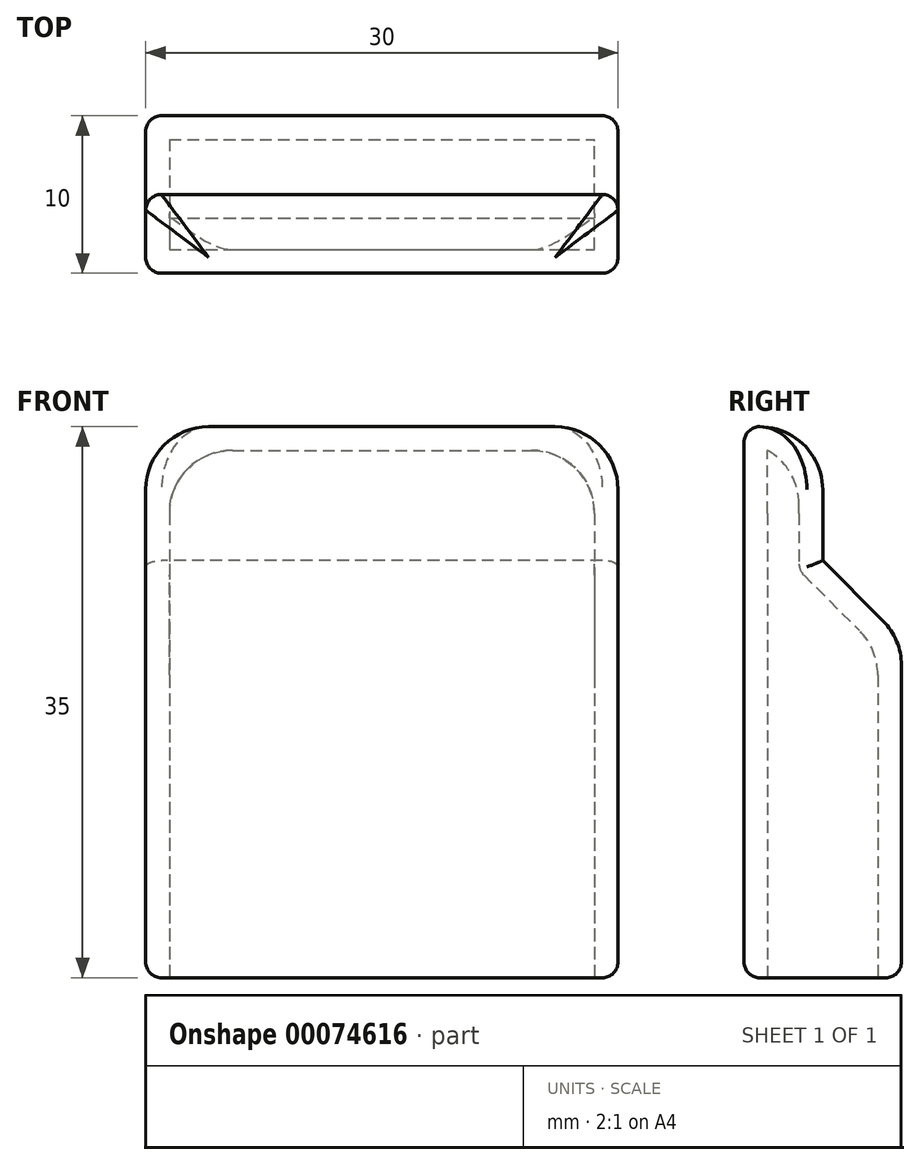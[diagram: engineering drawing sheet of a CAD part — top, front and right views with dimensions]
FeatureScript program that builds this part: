
annotation { "Feature Type Name" : "Feature", "Feature Type Description" : "" }
export const myFeature = defineFeature(function(context is Context, id is Id, definition is map)
    precondition{}
    {
        {
            var Q0;
            Q0=qCreatedBy(makeId("Top.planeOp"),FACE);
            var sketch = newSketch(context, id + "F0", { "sketchPlane" : qUnion([Q0])});
            skLineSegment(sketch, "E0", {"start": v(0, 0) * mm, "end": v(30, 0) * mm});
            skLineSegment(sketch, "E1", {"start": v(30, 0) * mm, "end": v(30, 5) * mm});
            skLineSegment(sketch, "E2", {"start": v(30, 5) * mm, "end": v(0, 5) * mm});
            skLineSegment(sketch, "E3", {"start": v(0, 5) * mm, "end": v(0, 0) * mm});
            skLineSegment(sketch, "E4", {"start": v(0, 5) * mm, "end": v(0, 10) * mm});
            skLineSegment(sketch, "E5", {"start": v(0, 10) * mm, "end": v(30, 10) * mm});
            skLineSegment(sketch, "E6", {"start": v(30, 10) * mm, "end": v(30, 5) * mm});
            skSolve(sketch);
        }
        {
            var Q0;
            Q0=makeQuery(id+"F0.imprint","IMPRINT",FACE,{"disambiguationData":[TD([[makeQuery(id+"F0.imprint","IMPRINT",EDGE,{"derivedFrom":sQuery(id+"F0.wireOp",EDGE,"E0")}),1.0]])]});
            extrude(context, id + "F1", {"entities" : qUnion([Q0]), "depth" : 35 * mm});
        }
        {
            var Q0;
            Q0=makeQuery(id+"F0.imprint","IMPRINT",FACE,{"disambiguationData":[TD([[makeQuery(id+"F0.imprint","IMPRINT",EDGE,{"derivedFrom":sQuery(id+"F0.wireOp",EDGE,"E2")}),-1.0]])]});
            extrude(context, id + "F2", {"entities" : qUnion([Q0]), "operationType" : NewBodyOperationType.ADD, "depth" : 26.5 * mm});
        }
        {
            var Q0;
            Q0=makeQuery(id+"F2.opExtrude","CAP_EDGE",EDGE,{"disambiguationData":[OSD([sQuery(id+"F0.wireOp",EDGE,"E5")])],"isStart":false});
            chamfer(context, id + "F3", {"entities" : qUnion([Q0]), "width" : 5 * mm, "tangentPropagation" : true});
        }
        {
            var Q0;
            {var subQ0=sQuery(id+"F0.wireOp",EDGE,"E2");Q0=makeQuery(id+"F2.boolean.opBoolean","MERGE",FACE,{"derivedFrom":[makeQuery(id+"F1.opExtrude","CAP_FACE",FACE,{"disambiguationData":[OSD([sQuery(id+"F0.wireOp",EDGE,"E0"),sQuery(id+"F0.wireOp",EDGE,"E1"),subQ0,sQuery(id+"F0.wireOp",EDGE,"E3")])],"isStart":true}),makeQuery(id+"F2.opExtrude","CAP_FACE",FACE,{"disambiguationData":[OSD([subQ0,sQuery(id+"F0.wireOp",EDGE,"E4"),sQuery(id+"F0.wireOp",EDGE,"E5"),sQuery(id+"F0.wireOp",EDGE,"E6")])],"isStart":true})]});}
            shell(context, id + "F4", {"entities" : qUnion([Q0]), "thickness" : 1.5 * mm});
        }
        {
            var Q0;
            Q0=makeQuery(id+"F1.opExtrude","CAP_EDGE",EDGE,{"disambiguationData":[OSD([sQuery(id+"F0.wireOp",EDGE,"E1")])],"isStart":false});
            var Q1;
            Q1=makeQuery(id+"F1.opExtrude","CAP_EDGE",EDGE,{"disambiguationData":[OSD([sQuery(id+"F0.wireOp",EDGE,"E3")])],"isStart":false});
            var Q2;
            {var subQ0=sQuery(id+"F0.wireOp",EDGE,"E5");Q2=makeQuery(id+"F3.opChamfer","BLEND_EDGE",EDGE,{"blendedFrom":[makeQuery(id+"F2.opExtrude","CAP_EDGE",EDGE,{"disambiguationData":[OSD([subQ0])],"isStart":false}),makeQuery(id+"F2.opExtrude","SWEPT_FACE",FACE,{"disambiguationData":[OSD([subQ0])]})],"blendedInto":[makeQuery(id+"F2.opExtrude","SWEPT_FACE",FACE,{"disambiguationData":[OSD([subQ0])]})]});}
            var Q3;
            {var subQ0=sQuery(id+"F0.wireOp",EDGE,"E5");Q3=makeQuery(id+"F4.opShell","OFFSET_EDGE",EDGE,{"disambiguationData":[OSD([subQ0]),TDD([makeQuery(id+"F3.opChamfer","BLEND_EDGE",EDGE,{"blendedFrom":[makeQuery(id+"F2.opExtrude","CAP_EDGE",EDGE,{"disambiguationData":[OSD([subQ0])],"isStart":false}),makeQuery(id+"F2.opExtrude","SWEPT_FACE",FACE,{"disambiguationData":[OSD([subQ0])]})],"blendedInto":[makeQuery(id+"F2.opExtrude","SWEPT_FACE",FACE,{"disambiguationData":[OSD([subQ0])]})]})])]});}
            var Q4;
            Q4=makeQuery(id+"F4.opShell","OFFSET_EDGE",EDGE,{"disambiguationData":[OSD([sQuery(id+"F0.wireOp",EDGE,"E1")])]});
            var Q5;
            Q5=makeQuery(id+"F4.opShell","OFFSET_EDGE",EDGE,{"disambiguationData":[OSD([sQuery(id+"F0.wireOp",EDGE,"E3")])]});
            fillet(context, id + "F5", {"entities" : qUnion([Q0, Q1, Q2, Q3, Q4, Q5]), "radius" : 4 * mm, "tangentPropagation" : true, "allowEdgeOverflow" : false});
        }
        {
            var Q0;
            Q0=makeQuery(id+"F1.opExtrude","CAP_EDGE",EDGE,{"disambiguationData":[OSD([sQuery(id+"F0.wireOp",EDGE,"E2")])],"isStart":false});
            var Q1;
            Q1=makeQuery(id+"F4.opShell","OFFSET_EDGE",EDGE,{"disambiguationData":[OSD([sQuery(id+"F0.wireOp",EDGE,"E2")])]});
            fillet(context, id + "F6", {"entities" : qUnion([Q0, Q1]), "radius" : 4 * mm, "allowEdgeOverflow" : false});
        }
        {
            var Q0;
            Q0=makeQuery(id+"F1.opExtrude","CAP_EDGE",EDGE,{"disambiguationData":[OSD([sQuery(id+"F0.wireOp",EDGE,"E0")])],"isStart":false});
            var Q1;
            Q1=makeQuery(id+"F5.opFillet","BLEND_EDGE",EDGE,{"blendedFrom":[makeQuery(id+"F1.opExtrude","CAP_EDGE",EDGE,{"disambiguationData":[OSD([sQuery(id+"F0.wireOp",EDGE,"E1")])],"isStart":false}),makeQuery(id+"F1.opExtrude","SWEPT_FACE",FACE,{"disambiguationData":[OSD([sQuery(id+"F0.wireOp",EDGE,"E0")])]})],"blendedInto":[makeQuery(id+"F1.opExtrude","SWEPT_FACE",FACE,{"disambiguationData":[OSD([sQuery(id+"F0.wireOp",EDGE,"E0")])]})]});
            var Q2;
            {var subQ0=sQuery(id+"F0.wireOp",EDGE,"E1");Q2=makeQuery(id+"F6.opFillet","BLEND_EDGE",EDGE,{"blendedFrom":[makeQuery(id+"F1.opExtrude","CAP_EDGE",EDGE,{"disambiguationData":[OSD([sQuery(id+"F0.wireOp",EDGE,"E2")])],"isStart":false}),makeQuery(id+"F5.opFillet","BLEND_FACE",FACE,{"disambiguationData":[OSD([subQ0]),TDD([makeQuery(id+"F1.opExtrude","CAP_EDGE",EDGE,{"disambiguationData":[OSD([subQ0])],"isStart":false})])]})],"blendedInto":[makeQuery(id+"F5.opFillet","BLEND_FACE",FACE,{"disambiguationData":[OSD([subQ0]),TDD([makeQuery(id+"F1.opExtrude","CAP_EDGE",EDGE,{"disambiguationData":[OSD([subQ0])],"isStart":false})])]})]});}
            var Q3;
            Q3=makeQuery(id+"F3.opChamfer","BLEND_EDGE",EDGE,{"blendedFrom":[makeQuery(id+"F2.opExtrude","CAP_EDGE",EDGE,{"disambiguationData":[OSD([sQuery(id+"F0.wireOp",EDGE,"E5")])],"isStart":false}),makeQuery(id+"F2.boolean.opBoolean","MERGE",FACE,{"derivedFrom":[makeQuery(id+"F1.opExtrude","SWEPT_FACE",FACE,{"disambiguationData":[OSD([sQuery(id+"F0.wireOp",EDGE,"E1")])]}),makeQuery(id+"F2.opExtrude","SWEPT_FACE",FACE,{"disambiguationData":[OSD([sQuery(id+"F0.wireOp",EDGE,"E6")])]})]})],"blendedInto":[makeQuery(id+"F2.boolean.opBoolean","MERGE",FACE,{"derivedFrom":[makeQuery(id+"F1.opExtrude","SWEPT_FACE",FACE,{"disambiguationData":[OSD([sQuery(id+"F0.wireOp",EDGE,"E1")])]}),makeQuery(id+"F2.opExtrude","SWEPT_FACE",FACE,{"disambiguationData":[OSD([sQuery(id+"F0.wireOp",EDGE,"E6")])]})]})]});
            var Q4;
            Q4=makeQuery(id+"F2.boolean.opBoolean","MERGE",EDGE,{"derivedFrom":[makeQuery(id+"F1.opExtrude","CAP_EDGE",EDGE,{"disambiguationData":[OSD([sQuery(id+"F0.wireOp",EDGE,"E1")])],"isStart":true}),makeQuery(id+"F2.opExtrude","CAP_EDGE",EDGE,{"disambiguationData":[OSD([sQuery(id+"F0.wireOp",EDGE,"E6")])],"isStart":true})]});
            var Q5;
            {var subQ0=sQuery(id+"F0.wireOp",EDGE,"E3");Q5=makeQuery(id+"F6.opFillet","BLEND_EDGE",EDGE,{"blendedFrom":[makeQuery(id+"F1.opExtrude","CAP_EDGE",EDGE,{"disambiguationData":[OSD([sQuery(id+"F0.wireOp",EDGE,"E2")])],"isStart":false}),makeQuery(id+"F5.opFillet","BLEND_FACE",FACE,{"disambiguationData":[OSD([subQ0]),TDD([makeQuery(id+"F1.opExtrude","CAP_EDGE",EDGE,{"disambiguationData":[OSD([subQ0])],"isStart":false})])]})],"blendedInto":[makeQuery(id+"F5.opFillet","BLEND_FACE",FACE,{"disambiguationData":[OSD([subQ0]),TDD([makeQuery(id+"F1.opExtrude","CAP_EDGE",EDGE,{"disambiguationData":[OSD([subQ0])],"isStart":false})])]})]});}
            var Q6;
            Q6=makeQuery(id+"F3.opChamfer","BLEND_EDGE",EDGE,{"blendedFrom":[makeQuery(id+"F2.opExtrude","CAP_EDGE",EDGE,{"disambiguationData":[OSD([sQuery(id+"F0.wireOp",EDGE,"E5")])],"isStart":false}),makeQuery(id+"F2.boolean.opBoolean","MERGE",FACE,{"derivedFrom":[makeQuery(id+"F1.opExtrude","SWEPT_FACE",FACE,{"disambiguationData":[OSD([sQuery(id+"F0.wireOp",EDGE,"E3")])]}),makeQuery(id+"F2.opExtrude","SWEPT_FACE",FACE,{"disambiguationData":[OSD([sQuery(id+"F0.wireOp",EDGE,"E4")])]})]})],"blendedInto":[makeQuery(id+"F2.boolean.opBoolean","MERGE",FACE,{"derivedFrom":[makeQuery(id+"F1.opExtrude","SWEPT_FACE",FACE,{"disambiguationData":[OSD([sQuery(id+"F0.wireOp",EDGE,"E3")])]}),makeQuery(id+"F2.opExtrude","SWEPT_FACE",FACE,{"disambiguationData":[OSD([sQuery(id+"F0.wireOp",EDGE,"E4")])]})]})]});
            var Q7;
            Q7=makeQuery(id+"F2.boolean.opBoolean","MERGE",EDGE,{"derivedFrom":[makeQuery(id+"F1.opExtrude","CAP_EDGE",EDGE,{"disambiguationData":[OSD([sQuery(id+"F0.wireOp",EDGE,"E3")])],"isStart":true}),makeQuery(id+"F2.opExtrude","CAP_EDGE",EDGE,{"disambiguationData":[OSD([sQuery(id+"F0.wireOp",EDGE,"E4")])],"isStart":true})]});
            var Q8;
            Q8=makeQuery(id+"F2.opExtrude","CAP_EDGE",EDGE,{"disambiguationData":[OSD([sQuery(id+"F0.wireOp",EDGE,"E5")])],"isStart":true});
            var Q9;
            Q9=makeQuery(id+"F1.opExtrude","CAP_EDGE",EDGE,{"disambiguationData":[OSD([sQuery(id+"F0.wireOp",EDGE,"E0")])],"isStart":true});
            var Q10;
            Q10=makeQuery(id+"F4.opShell","OFFSET_EDGE",EDGE,{"disambiguationData":[OSD([sQuery(id+"F0.wireOp",EDGE,"E2"),sQuery(id+"F0.wireOp",EDGE,"E5")])]});
            fillet(context, id + "F7", {"entities" : qUnion([Q0, Q1, Q2, Q3, Q4, Q5, Q6, Q7, Q8, Q9, Q10]), "radius" : 1 * mm, "tangentPropagation" : true, "allowEdgeOverflow" : false});
        }
    });
